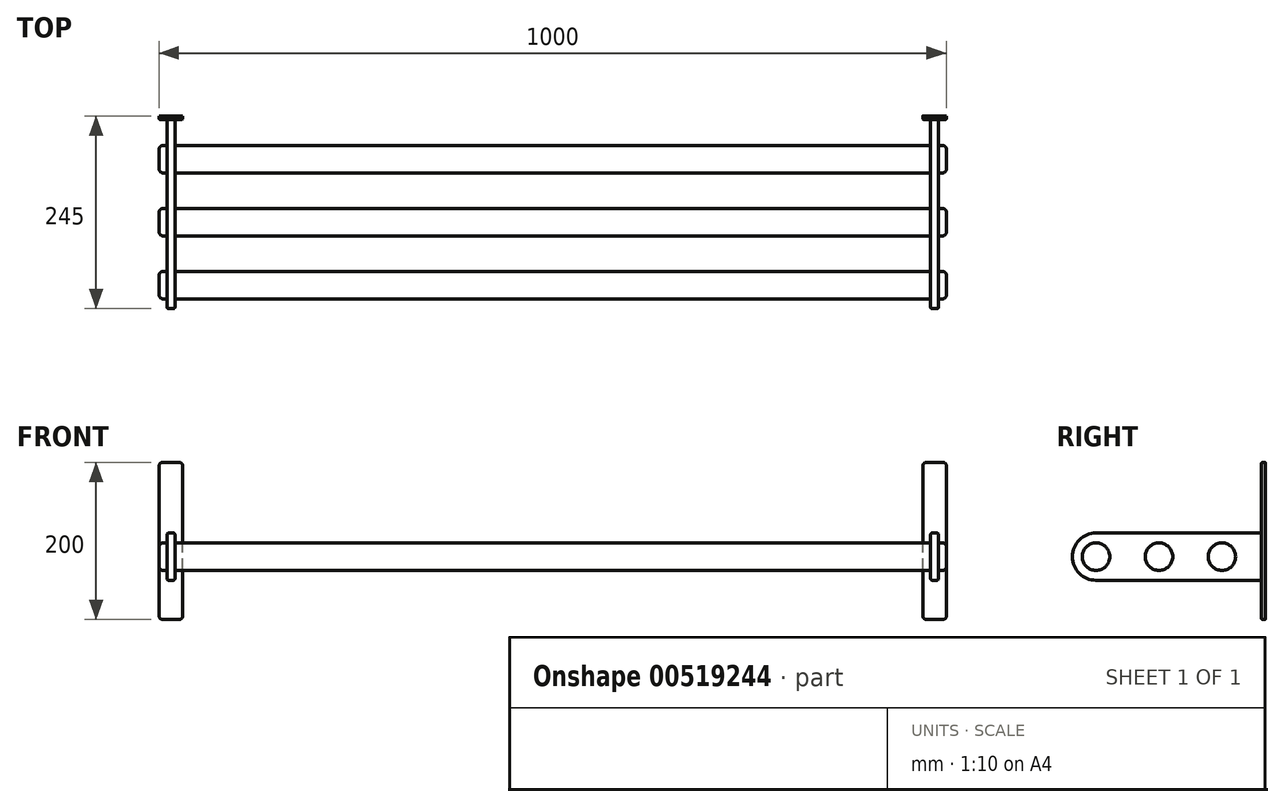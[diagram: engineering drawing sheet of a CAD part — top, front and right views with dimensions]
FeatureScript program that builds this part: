
annotation { "Feature Type Name" : "Feature", "Feature Type Description" : "" }
export const myFeature = defineFeature(function(context is Context, id is Id, definition is map)
    precondition{}
    {
        {
            var Q0;
            Q0=qCreatedBy(makeId("Right.planeOp"),FACE);
            var sketch = newSketch(context, id + "F0", { "sketchPlane" : qUnion([Q0])});
            skLineSegment(sketch, "E0.bottom", {"start": v(0, 0) * mm, "end": v(5, 0) * mm});
            skLineSegment(sketch, "E0.top", {"start": v(0, 200) * mm, "end": v(5, 200) * mm});
            skLineSegment(sketch, "E0.left", {"start": v(0, 0) * mm, "end": v(0, 200) * mm});
            skLineSegment(sketch, "E0.right", {"start": v(5, 0) * mm, "end": v(5, 200) * mm});
            skSolve(sketch);
        }
        {
            var Q0;
            Q0 = qSketchRegion(id + "F0", true);
            extrude(context, id + "F1", {"entities" : qUnion([Q0]), "depth" : 30 * mm, "offsetDistance" : 25 * mm});
        }
        {
            var Q0;
            Q0=makeQuery(id+"F1.opExtrude","SWEPT_FACE",FACE,{"disambiguationData":[OSD([sQuery(id+"F0.wireOp",EDGE,"E0.left")])]});
            var sketch = newSketch(context, id + "F2", { "sketchPlane" : qUnion([Q0])});
            skLineSegment(sketch, "E1.bottom", {"start": v(10, 110) * mm, "end": v(20, 110) * mm});
            skLineSegment(sketch, "E1.top", {"start": v(10, 50) * mm, "end": v(20, 50) * mm});
            skLineSegment(sketch, "E1.left", {"start": v(10, 110) * mm, "end": v(10, 50) * mm});
            skLineSegment(sketch, "E1.right", {"start": v(20, 110) * mm, "end": v(20, 50) * mm});
            skSolve(sketch);
        }
        {
            var Q0;
            Q0 = qSketchRegion(id + "F2", true);
            extrude(context, id + "F3", {"entities" : qUnion([Q0]), "operationType" : NewBodyOperationType.ADD, "depth" : 240 * mm, "offsetDistance" : 25 * mm});
        }
        {
            var Q0;
            Q0=makeQuery(id+"F3.opExtrude","CAP_EDGE",EDGE,{"disambiguationData":[OSD([sQuery(id+"F2.wireOp",EDGE,"E1.bottom")])],"isStart":false});
            var Q1;
            Q1=makeQuery(id+"F3.opExtrude","CAP_EDGE",EDGE,{"disambiguationData":[OSD([sQuery(id+"F2.wireOp",EDGE,"E1.top")])],"isStart":false});
            fillet(context, id + "F4", {"entities" : qUnion([Q0, Q1]), "radius" : 30 * mm, "tangentPropagation" : true, "allowEdgeOverflow" : false});
        }
        {
            var Q0;
            Q0=makeQuery(id+"F3.opExtrude","SWEPT_FACE",FACE,{"disambiguationData":[OSD([sQuery(id+"F2.wireOp",EDGE,"E1.left")])]});
            var sketch = newSketch(context, id + "F5", { "sketchPlane" : qUnion([Q0])});
            skLineSegment(sketch, "E2", {"start": v(0, 80) * mm, "end": v(240, 80) * mm, "construction": true});
            skCircle(sketch, "E3", {"center": v(210, 80) * mm, "radius": 17.5 * mm});
            skCircle(sketch, "E4.1.0.0", {"center": v(130, 80) * mm, "radius": 17.5 * mm});
            skCircle(sketch, "E4.2.0.0", {"center": v(50, 80) * mm, "radius": 17.5 * mm});
            skLineSegment(sketch, "E4.direction1", {"start": v(210, 80) * mm, "end": v(130, 80) * mm, "construction": true});
            skSolve(sketch);
        }
        {
            var Q0;
            Q0 = qSketchRegion(id + "F5", true);
            extrude(context, id + "F6", {"entities" : qUnion([Q0]), "operationType" : NewBodyOperationType.ADD, "depth" : 10 * mm, "offsetDistance" : 25 * mm});
        }
        {
            var Q0;
            Q0=makeQuery(id+"F3.opExtrude","SWEPT_FACE",FACE,{"disambiguationData":[OSD([sQuery(id+"F2.wireOp",EDGE,"E1.left")])]});
            var sketch = newSketch(context, id + "F7", { "sketchPlane" : qUnion([Q0])});
            skCircle(sketch, "E5.0.0", {"center": v(50, 80) * mm, "radius": 17.5 * mm});
            skCircle(sketch, "E6.0.0", {"center": v(130, 80) * mm, "radius": 17.5 * mm});
            skCircle(sketch, "E7.0.0", {"center": v(210, 80) * mm, "radius": 17.5 * mm});
            skSolve(sketch);
        }
        {
            var Q0;
            Q0 = qSketchRegion(id + "F7", true);
            extrude(context, id + "F8", {"entities" : qUnion([Q0]), "operationType" : NewBodyOperationType.ADD, "oppositeDirection" : true, "depth" : 490 * mm, "offsetDistance" : 25 * mm});
        }
        {
            var Q0;
            Q0=makeQuery(id+"F6.opExtrude","CAP_FACE",FACE,{"disambiguationData":[OSD([sQuery(id+"F5.wireOp",EDGE,"E3")])],"isStart":false});
            var Q1;
            Q1=makeQuery(id+"F6.opExtrude","CAP_FACE",FACE,{"disambiguationData":[OSD([sQuery(id+"F5.wireOp",EDGE,"E4.1.0.0")])],"isStart":false});
            var Q2;
            Q2=makeQuery(id+"F6.opExtrude","CAP_FACE",FACE,{"disambiguationData":[OSD([sQuery(id+"F5.wireOp",EDGE,"E4.2.0.0")])],"isStart":false});
            var Q3;
            Q3=makeQuery(id+"F1.opExtrude","CAP_EDGE",EDGE,{"disambiguationData":[OSD([sQuery(id+"F0.wireOp",EDGE,"E0.bottom")])],"isStart":true});
            var Q4;
            Q4=makeQuery(id+"F1.opExtrude","CAP_EDGE",EDGE,{"disambiguationData":[OSD([sQuery(id+"F0.wireOp",EDGE,"E0.bottom")])],"isStart":false});
            var Q5;
            Q5=makeQuery(id+"F1.opExtrude","CAP_EDGE",EDGE,{"disambiguationData":[OSD([sQuery(id+"F0.wireOp",EDGE,"E0.top")])],"isStart":false});
            var Q6;
            Q6=makeQuery(id+"F1.opExtrude","CAP_EDGE",EDGE,{"disambiguationData":[OSD([sQuery(id+"F0.wireOp",EDGE,"E0.top")])],"isStart":true});
            fillet(context, id + "F9", {"entities" : qUnion([Q0, Q1, Q2, Q3, Q4, Q5, Q6]), "radius" : 5 * mm, "tangentPropagation" : true, "allowEdgeOverflow" : false});
        }
        {
            var Q0;
            Q0=makeQuery(id+"F1.opExtrude","SWEPT_FACE",FACE,{"disambiguationData":[OSD([sQuery(id+"F0.wireOp",EDGE,"E0.left")])]});
            var Q1;
            Q1=makeQuery(id+"F3.opExtrude","SWEPT_FACE",FACE,{"disambiguationData":[OSD([sQuery(id+"F2.wireOp",EDGE,"E1.left")])]});
            var Q2;
            Q2=makeQuery(id+"F3.opExtrude","SWEPT_FACE",FACE,{"disambiguationData":[OSD([sQuery(id+"F2.wireOp",EDGE,"E1.top")])]});
            fillet(context, id + "F10", {"entities" : qUnion([Q0, Q1, Q2]), "radius" : 2 * mm, "tangentPropagation" : true, "allowEdgeOverflow" : false});
        }
        {
            var Q0;
            Q0=qCreatedBy(makeId("Right.planeOp"),FACE);
            cPlane(context, id + "F11", {"entities" : qUnion([Q0]), "cplaneType" : CPlaneType.OFFSET, "offset" : 500 * mm, "width" : 150 * mm, "height" : 150 * mm});
        }
        {
            var Q0;
            Q0=makeQuery(id+"F1.opExtrude","SWEPT_BODY",BODY,{"disambiguationData":[OSD([sQuery(id+"F0.wireOp",EDGE,"E0.bottom"),sQuery(id+"F0.wireOp",EDGE,"E0.top"),sQuery(id+"F0.wireOp",EDGE,"E0.left"),sQuery(id+"F0.wireOp",EDGE,"E0.right")])]});
            var Q1;
            Q1=qCreatedBy(id+"F11.planeOp",FACE);
            mirror(context, id + "F12", {"operationType" : NewBodyOperationType.ADD, "entities" : qUnion([Q0]), "mirrorPlane" : qUnion([Q1])});
        }
    });
